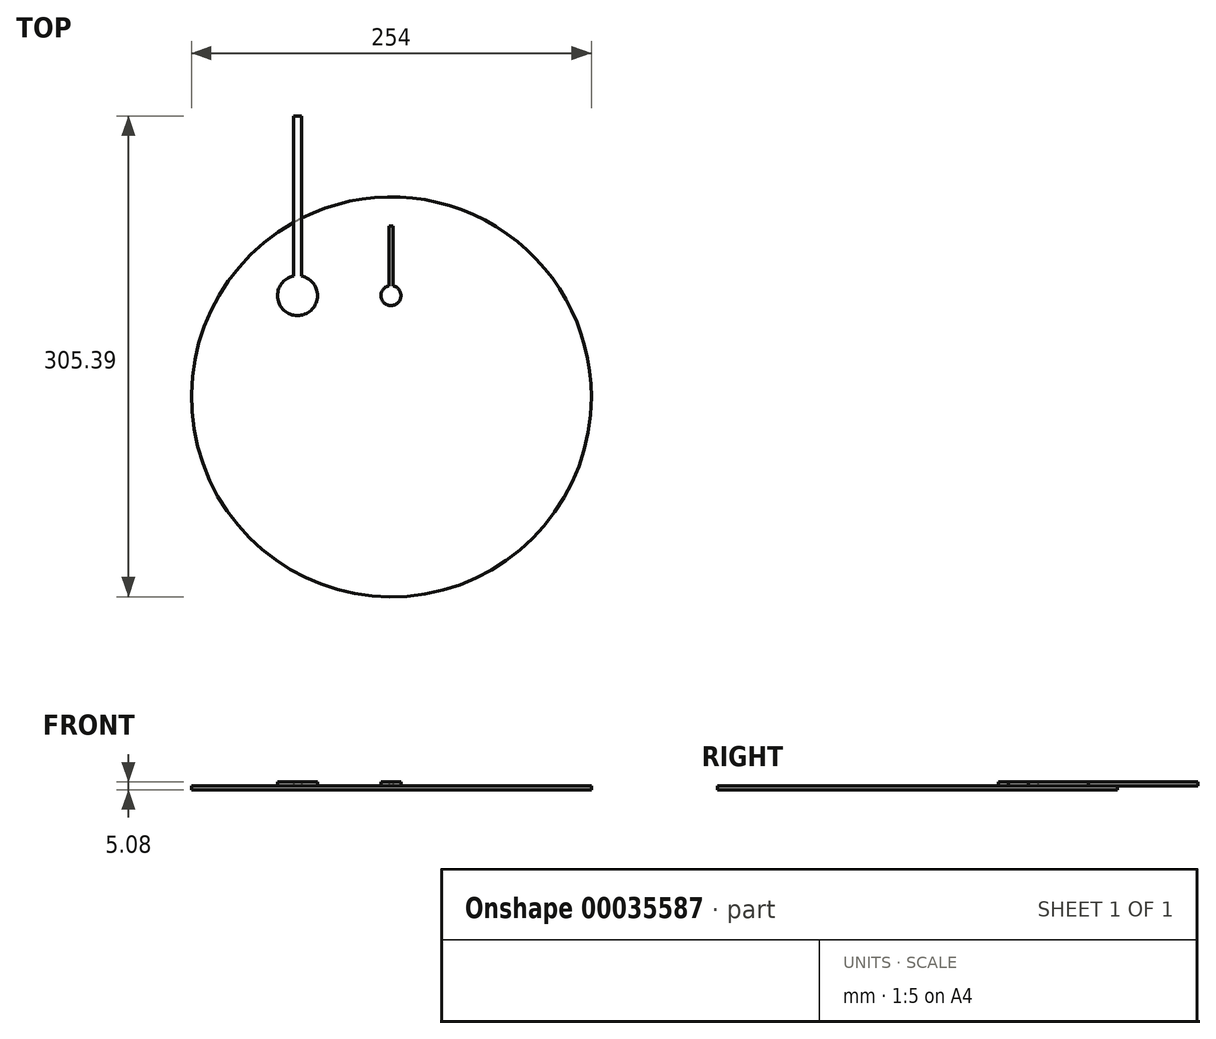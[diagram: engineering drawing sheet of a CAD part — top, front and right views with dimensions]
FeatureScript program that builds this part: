
annotation { "Feature Type Name" : "Feature", "Feature Type Description" : "" }
export const myFeature = defineFeature(function(context is Context, id is Id, definition is map)
    precondition{}
    {
        {
            var Q0;
            Q0=qCreatedBy(makeId("Top.planeOp"),FACE);
            var sketch = newSketch(context, id + "F0", { "sketchPlane" : qUnion([Q0])});
            skCircle(sketch, "E0", {"center": v(0, 0) * mm, "radius": 12.7 * mm});
            skLineSegment(sketch, "E1", {"start": v(-2.54, 12.44) * mm, "end": v(-2.54, 114.04) * mm});
            skLineSegment(sketch, "E2", {"start": v(-2.54, 114.04) * mm, "end": v(0, 114.04) * mm});
            skLineSegment(sketch, "E3", {"start": v(0, 120.9) * mm, "end": v(0, 60.73) * mm, "construction": true});
            skLineSegment(sketch, "E4.MirrorCS", {"start": v(2.54, 12.44) * mm, "end": v(2.54, 114.04) * mm});
            skLineSegment(sketch, "E5.MirrorCS", {"start": v(2.54, 114.04) * mm, "end": v(0, 114.04) * mm});
            skSolve(sketch);
        }
        {
            var Q0;
            {var subQ0=sQuery(id+"F0.wireOp",EDGE,"E0");var subQ2=makeQuery(id+"F0.imprint","INTERSECT",VERTEX,{"derivedFrom":[subQ0,sQuery(id+"F0.wireOp",EDGE,"E1")]});Q0=makeQuery(id+"F0.imprint","IMPRINT",FACE,{"disambiguationData":[TD([[makeQuery(id+"F0.imprint","IMPRINT",EDGE,{"disambiguationData":[TD([[subQ2,1.0]])],"derivedFrom":subQ0}),1.0]])]});}
            var Q1;
            {var subQ2=sQuery(id+"F0.wireOp",EDGE,"E1");Q1=makeQuery(id+"F0.imprint","IMPRINT",FACE,{"disambiguationData":[TD([[makeQuery(id+"F0.imprint","IMPRINT",EDGE,{"derivedFrom":subQ2}),-1.0]])]});}
            extrude(context, id + "F1", {"entities" : qUnion([Q0, Q1]), "depth" : 2.54 * mm});
        }
        {
            var Q0;
            Q0=qCreatedBy(makeId("Top.planeOp"),FACE);
            var sketch = newSketch(context, id + "F2", { "sketchPlane" : qUnion([Q0])});
            skCircle(sketch, "E6", {"center": v(59.33, 0) * mm, "radius": 6.35 * mm});
            skLineSegment(sketch, "E7", {"start": v(59.33, 0) * mm, "end": v(59.33, 46.77) * mm, "construction": true});
            skLineSegment(sketch, "E8", {"start": v(58.06, 6.22) * mm, "end": v(58.06, 44.32) * mm});
            skLineSegment(sketch, "E9", {"start": v(58.06, 44.32) * mm, "end": v(59.33, 44.32) * mm});
            skLineSegment(sketch, "E10.MirrorCS", {"start": v(60.6, 6.22) * mm, "end": v(60.6, 44.32) * mm});
            skLineSegment(sketch, "E11.MirrorCS", {"start": v(60.6, 44.32) * mm, "end": v(59.33, 44.32) * mm});
            skSolve(sketch);
        }
        {
            var Q0;
            {var subQ0=sQuery(id+"F2.wireOp",EDGE,"E6");var subQ2=makeQuery(id+"F2.imprint","INTERSECT",VERTEX,{"derivedFrom":[subQ0,sQuery(id+"F2.wireOp",EDGE,"E8")]});Q0=makeQuery(id+"F2.imprint","IMPRINT",FACE,{"disambiguationData":[TD([[makeQuery(id+"F2.imprint","IMPRINT",EDGE,{"disambiguationData":[TD([[subQ2,1.0]])],"derivedFrom":subQ0}),1.0]])]});}
            var Q1;
            {var subQ2=sQuery(id+"F2.wireOp",EDGE,"E8");Q1=makeQuery(id+"F2.imprint","IMPRINT",FACE,{"disambiguationData":[TD([[makeQuery(id+"F2.imprint","IMPRINT",EDGE,{"derivedFrom":subQ2}),-1.0]])]});}
            extrude(context, id + "F3", {"entities" : qUnion([Q0, Q1]), "depth" : 2.54 * mm});
        }
        {
            var Q0;
            Q0=qCreatedBy(makeId("Top.planeOp"),FACE);
            var sketch = newSketch(context, id + "F4", { "sketchPlane" : qUnion([Q0])});
            skCircle(sketch, "E12", {"center": v(59.59, -64.35) * mm, "radius": 127 * mm});
            skSolve(sketch);
        }
        {
            var Q0;
            Q0=makeQuery(id+"F4.imprint","IMPRINT",FACE,{"disambiguationData":[TD([[makeQuery(id+"F4.imprint","IMPRINT",EDGE,{"derivedFrom":sQuery(id+"F4.wireOp",EDGE,"E12")}),1.0]])]});
            extrude(context, id + "F5", {"entities" : qUnion([Q0]), "oppositeDirection" : true, "depth" : 2.54 * mm});
        }
    });
